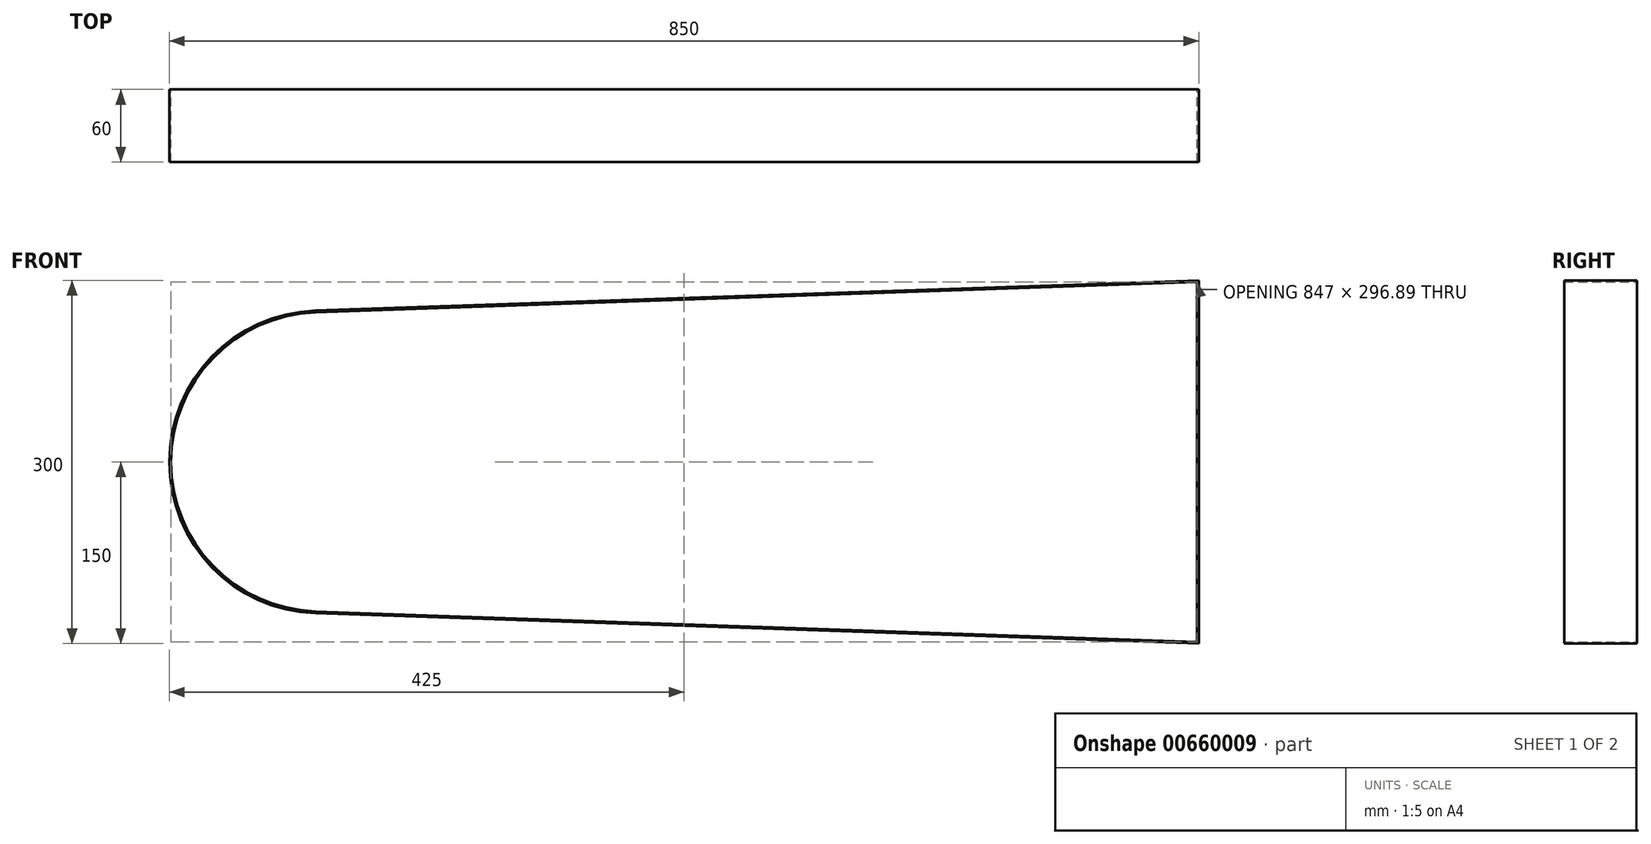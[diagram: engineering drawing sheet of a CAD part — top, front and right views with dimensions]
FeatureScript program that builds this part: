
annotation { "Feature Type Name" : "Feature", "Feature Type Description" : "" }
export const myFeature = defineFeature(function(context is Context, id is Id, definition is map)
    precondition{}
    {
        {
            var Q0;
            Q0=qCreatedBy(makeId("Front.planeOp"),FACE);
            var sketch = newSketch(context, id + "F0", { "sketchPlane" : qUnion([Q0])});
            skLineSegment(sketch, "E0", {"start": v(0, 0) * mm, "end": v(-725, 0) * mm});
            skLineSegment(sketch, "E1", {"start": v(0, 150) * mm, "end": v(-729.3, 124.93) * mm});
            skLineSegment(sketch, "E2", {"start": v(0, -150) * mm, "end": v(-729.3, -124.93) * mm});
            skLineSegment(sketch, "E3", {"start": v(0, 0) * mm, "end": v(0, 150) * mm});
            skLineSegment(sketch, "E4", {"start": v(0, 0) * mm, "end": v(0, -150) * mm});
            skArc(sketch, "E5", {"start": v(-729.3, 124.93) * mm, "mid": v(-850, 0) * mm, "end": v(-729.3, -124.93) * mm});
            skArc(sketch, "E6.0", {"start": v(-729.24, 123.43) * mm, "mid": v(-848.5, 0) * mm, "end": v(-729.24, -123.43) * mm});
            skLineSegment(sketch, "E6.1", {"start": v(-1.5, 148.45) * mm, "end": v(-729.24, 123.43) * mm});
            skLineSegment(sketch, "E6.2", {"start": v(-1.5, -148.45) * mm, "end": v(-729.24, -123.43) * mm});
            skLineSegment(sketch, "E6.3", {"start": v(-1.5, 0) * mm, "end": v(-1.5, -148.45) * mm});
            skLineSegment(sketch, "E6.4", {"start": v(-1.5, 0) * mm, "end": v(-1.5, 148.45) * mm});
            skSolve(sketch);
        }
        {
            var Q0;
            Q0=makeQuery(id+"F0.imprint","IMPRINT",FACE,{"disambiguationData":[TD([[makeQuery(id+"F0.imprint","IMPRINT",EDGE,{"derivedFrom":sQuery(id+"F0.wireOp",EDGE,"E1")}),1.0]])]});
            extrude(context, id + "F1", {"entities" : qUnion([Q0]), "depth" : 60 * mm, "offsetDistance" : 25 * mm});
        }
    });
